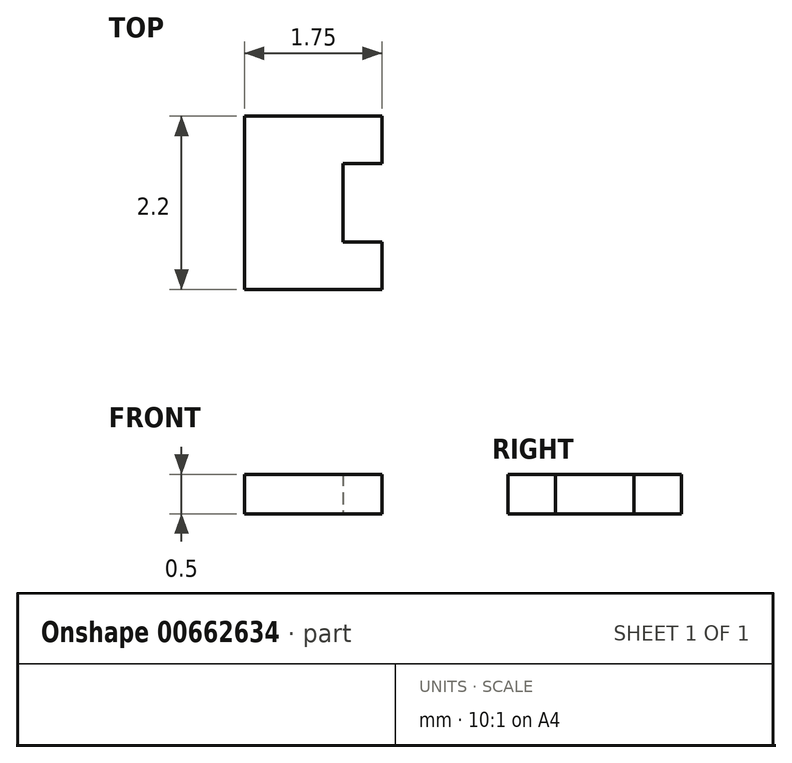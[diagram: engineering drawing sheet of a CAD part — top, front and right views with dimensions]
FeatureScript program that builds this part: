
annotation { "Feature Type Name" : "Feature", "Feature Type Description" : "" }
export const myFeature = defineFeature(function(context is Context, id is Id, definition is map)
    precondition{}
    {
        {
            var Q0;
            Q0=qCreatedBy(makeId("Top.planeOp"),FACE);
            var sketch = newSketch(context, id + "F0", { "sketchPlane" : qUnion([Q0])});
            skLineSegment(sketch, "E0.bottom", {"start": v(-1.5, 1.1) * mm, "end": v(0.25, 1.1) * mm});
            skLineSegment(sketch, "E0.top", {"start": v(-1.5, -1.1) * mm, "end": v(0.25, -1.1) * mm});
            skLineSegment(sketch, "E0.left", {"start": v(-1.5, 1.1) * mm, "end": v(-1.5, -1.1) * mm});
            skLineSegment(sketch, "E1", {"start": v(0.25, -0.5) * mm, "end": v(0.25, -1.1) * mm});
            skLineSegment(sketch, "E2.0", {"start": v(-0.25, 0.5) * mm, "end": v(-0.25, -0.5) * mm});
            skLineSegment(sketch, "E3.0", {"start": v(-0.25, 0.5) * mm, "end": v(0.25, 0.5) * mm});
            skLineSegment(sketch, "E4.0", {"start": v(-0.25, -0.5) * mm, "end": v(0.25, -0.5) * mm});
            skLineSegment(sketch, "E5", {"start": v(0.25, 0.5) * mm, "end": v(0.25, 1.1) * mm});
            skSolve(sketch);
        }
        {
            var Q0;
            Q0=makeQuery(id+"F0.imprint","IMPRINT",FACE,{"disambiguationData":[TD([[makeQuery(id+"F0.imprint","IMPRINT",EDGE,{"derivedFrom":sQuery(id+"F0.wireOp",EDGE,"E0.bottom")}),-1.0]])]});
            extrude(context, id + "F1", {"entities" : qUnion([Q0]), "depth" : .5 * mm, "offsetDistance" : 25 * mm});
        }
    });
